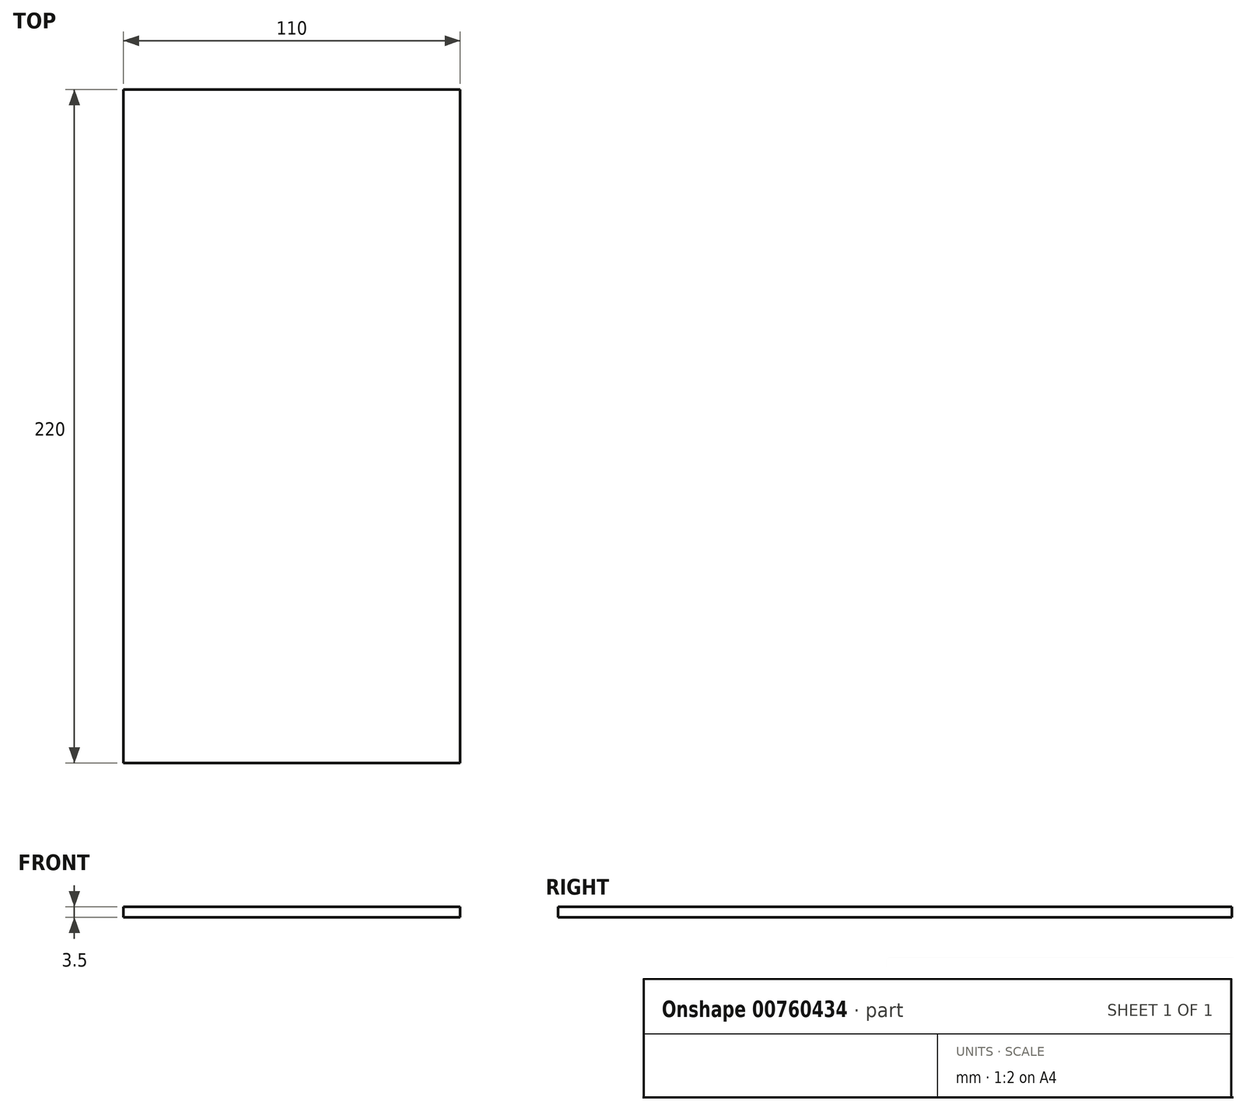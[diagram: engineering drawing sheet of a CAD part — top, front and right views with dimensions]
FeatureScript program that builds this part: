
annotation { "Feature Type Name" : "Feature", "Feature Type Description" : "" }
export const myFeature = defineFeature(function(context is Context, id is Id, definition is map)
    precondition{}
    {
        {
            var Q0;
            Q0=qCreatedBy(makeId("Top.planeOp"),FACE);
            var sketch = newSketch(context, id + "F0", { "sketchPlane" : qUnion([Q0])});
            skLineSegment(sketch, "E0.bottom", {"start": v(55, 110) * mm, "end": v(-55, 110) * mm});
            skLineSegment(sketch, "E0.top", {"start": v(55, -110) * mm, "end": v(-55, -110) * mm});
            skLineSegment(sketch, "E0.left", {"start": v(55, 110) * mm, "end": v(55, -110) * mm});
            skLineSegment(sketch, "E0.right", {"start": v(-55, 110) * mm, "end": v(-55, -110) * mm});
            skPoint(sketch, "E0.middle", {"position": v(0, 0) * mm});
            skSolve(sketch);
        }
        {
            var Q0;
            Q0 = qSketchRegion(id + "F0", true);
            extrude(context, id + "F1", {"entities" : qUnion([Q0]), "depth" : 3.5 * mm, "offsetDistance" : 25 * mm});
        }
    });
